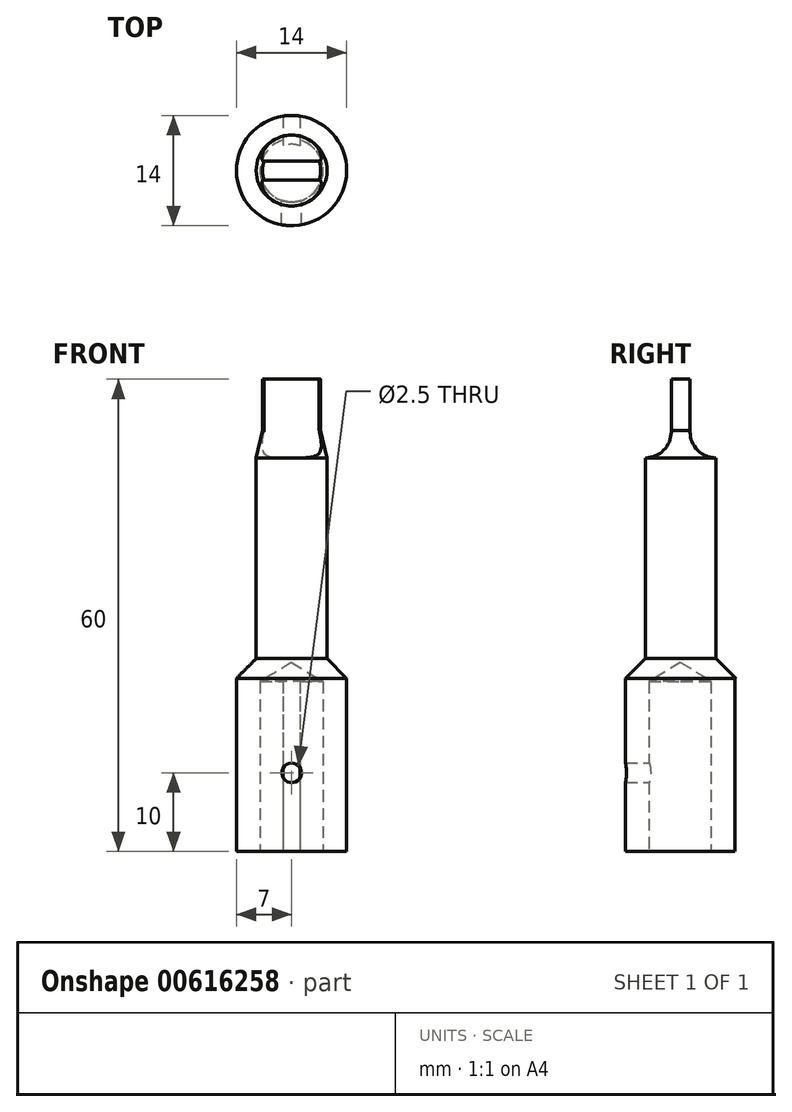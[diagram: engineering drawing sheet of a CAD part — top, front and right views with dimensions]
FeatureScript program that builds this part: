
annotation { "Feature Type Name" : "Feature", "Feature Type Description" : "" }
export const myFeature = defineFeature(function(context is Context, id is Id, definition is map)
    precondition{}
    {
        {
            var Q0;
            Q0=qCreatedBy(makeId("Front.planeOp"),FACE);
            var sketch = newSketch(context, id + "F0", { "sketchPlane" : qUnion([Q0])});
            skLineSegment(sketch, "E0", {"start": v(0, 0) * mm, "end": v(0, 60) * mm});
            skLineSegment(sketch, "E1", {"start": v(0, 60) * mm, "end": v(3.7, 60) * mm});
            skLineSegment(sketch, "E2", {"start": v(3.7, 60) * mm, "end": v(3.7, 53.5) * mm});
            skLineSegment(sketch, "E3", {"start": v(4.5, 50) * mm, "end": v(4.5, 24.5) * mm});
            skLineSegment(sketch, "E4", {"start": v(7, 22) * mm, "end": v(7, 0) * mm});
            skLineSegment(sketch, "E5", {"start": v(7, 0) * mm, "end": v(0, 0) * mm});
            skLineSegment(sketch, "E6", {"start": v(4.5, 50) * mm, "end": v(3.7, 53.5) * mm});
            skLineSegment(sketch, "E7", {"start": v(0, 0) * mm, "end": v(0, 83.24) * mm, "construction": true});
            skLineSegment(sketch, "E8", {"start": v(7, 22) * mm, "end": v(4.5, 24.5) * mm});
            skSolve(sketch);
        }
        {
            var Q0;
            Q0=makeQuery(id+"F0.imprint","IMPRINT",FACE,{"disambiguationData":[TD([[makeQuery(id+"F0.imprint","IMPRINT",EDGE,{"derivedFrom":sQuery(id+"F0.wireOp",EDGE,"E0")}),-1.0]])]});
            var Q1;
            Q1=sQuery(id+"F0.wireOp",EDGE,"E7");
            revolve(context, id + "F1", {"entities" : qUnion([Q0]), "axis" : qUnion([Q1]), "revolveType" : RevolveType.FULL});
        }
        {
            var Q0;
            Q0=makeQuery(id+"F1.opRevolve","SWEPT_FACE",FACE,{"disambiguationData":[OSD([sQuery(id+"F0.wireOp",EDGE,"E5")])]});
            var sketch = newSketch(context, id + "F2", { "sketchPlane" : qUnion([Q0])});
            skPoint(sketch, "E9", {"position": v(0, 0) * mm});
            skSolve(sketch);
        }
        {
            var Q0;
            Q0=sQuery(id+"F2.wireOp",VERTEX,"E9");
            var Q1;
            Q1=makeQuery(id+"F1.opRevolve","SWEPT_BODY",BODY,{"disambiguationData":[OSD([sQuery(id+"F0.wireOp",EDGE,"E0"),sQuery(id+"F0.wireOp",EDGE,"E1"),sQuery(id+"F0.wireOp",EDGE,"E2"),sQuery(id+"F0.wireOp",EDGE,"E3"),sQuery(id+"F0.wireOp",EDGE,"E4"),sQuery(id+"F0.wireOp",EDGE,"E5"),sQuery(id+"F0.wireOp",EDGE,"E6"),sQuery(id+"F0.wireOp",EDGE,"a6a139c0-5f27-4006-9743-78f47c573285.filletArc")])]});
            hole(context, id + "F3", {"style" : HoleStyle.SIMPLE, "endStyle" : HoleEndStyle.BLIND, "standardTappedOrClearance" : lookupTablePath({ "standard" : "ISO", "size" : "8", "type" : "Drilled" }), "standardBlindInLast" : lookupTablePath({ "standard" : "ISO", "size" : "8", "type" : "Drilled" }), "holeDiameter" : 8 * mm, "majorDiameter" : 5 * mm, "holeDepth" : 21.6 * mm, "isTappedThrough" : true, "tappedDepth" : 18.6 * mm, "tapClearance" : 3, "startFromSketch" : true, "locations" : qUnion([Q0]), "scope" : qUnion([Q1])});
        }
        {
            var Q0;
            Q0=qCreatedBy(makeId("Front.planeOp"),FACE);
            var sketch = newSketch(context, id + "F4", { "sketchPlane" : qUnion([Q0])});
            skLineSegment(sketch, "E10.bottom", {"start": v(1.1, 0) * mm, "end": v(-1.1, 0) * mm});
            skLineSegment(sketch, "E10.top", {"start": v(1.1, 22) * mm, "end": v(-1.1, 22) * mm});
            skLineSegment(sketch, "E10.left", {"start": v(1.1, 0) * mm, "end": v(1.1, 22) * mm});
            skLineSegment(sketch, "E10.right", {"start": v(-1.1, 0) * mm, "end": v(-1.1, 22) * mm});
            skPoint(sketch, "E11", {"position": v(0, 0) * mm});
            skSolve(sketch);
        }
        {
            var Q0;
            Q0 = qSketchRegion(id + "F4", true);
            extrude(context, id + "F5", {"entities" : qUnion([Q0]), "operationType" : NewBodyOperationType.REMOVE, "endBound" : BoundingType.THROUGH_ALL, "oppositeDirection" : true, "depth" : 25 * mm, "offsetDistance" : 25 * mm});
        }
        {
            var Q0;
            Q0=qCreatedBy(makeId("Front.planeOp"),FACE);
            var sketch = newSketch(context, id + "F6", { "sketchPlane" : qUnion([Q0])});
            skPoint(sketch, "E12", {"position": v(0, 10) * mm});
            skSolve(sketch);
        }
        {
            var Q0;
            Q0=sQuery(id+"F6.wireOp",VERTEX,"E12");
            var Q1;
            Q1=makeQuery(id+"F1.opRevolve","SWEPT_BODY",BODY,{"disambiguationData":[OSD([sQuery(id+"F0.wireOp",EDGE,"E0"),sQuery(id+"F0.wireOp",EDGE,"E1"),sQuery(id+"F0.wireOp",EDGE,"E2"),sQuery(id+"F0.wireOp",EDGE,"E3"),sQuery(id+"F0.wireOp",EDGE,"E4"),sQuery(id+"F0.wireOp",EDGE,"E5"),sQuery(id+"F0.wireOp",EDGE,"E6"),sQuery(id+"F0.wireOp",EDGE,"E8")])]});
            hole(context, id + "F7", {"style" : HoleStyle.SIMPLE, "endStyle" : HoleEndStyle.THROUGH, "oppositeDirection" : true, "holeDiameter" : 2.5 * mm, "majorDiameter" : 5 * mm, "isTappedThrough" : true, "tappedDepth" : 18.6 * mm, "tapClearance" : 3, "startFromSketch" : true, "locations" : qUnion([Q0]), "scope" : qUnion([Q1])});
        }
        {
            var Q0;
            Q0=qCreatedBy(makeId("Right.planeOp"),FACE);
            var sketch = newSketch(context, id + "F8", { "sketchPlane" : qUnion([Q0])});
            skLineSegment(sketch, "E13", {"start": v(0, 60.47) * mm, "end": v(0, 49.01) * mm, "construction": true});
            skLineSegment(sketch, "E14", {"start": v(1.2, 60) * mm, "end": v(1.2, 53.3) * mm});
            skLineSegment(sketch, "E15", {"start": v(4.5, 50) * mm, "end": v(6.91, 50) * mm});
            skLineSegment(sketch, "E16", {"start": v(6.91, 50) * mm, "end": v(6.91, 60) * mm});
            skLineSegment(sketch, "E17", {"start": v(6.91, 60) * mm, "end": v(1.2, 60) * mm});
            skPoint(sketch, "E18.visualSharp", {"position": v(1.2, 50) * mm});
            skArc(sketch, "E18.filletArc", {"start": v(1.2, 53.3) * mm, "mid": v(2.17, 50.97) * mm, "end": v(4.5, 50) * mm});
            skPoint(sketch, "E19.MirrorP", {"position": v(-1.2, 50) * mm});
            skLineSegment(sketch, "E20.MirrorCS", {"start": v(-1.2, 60) * mm, "end": v(-1.2, 53.3) * mm});
            skLineSegment(sketch, "E21.MirrorCS", {"start": v(-4.5, 50) * mm, "end": v(-6.91, 50) * mm});
            skLineSegment(sketch, "E22.MirrorCS", {"start": v(-6.91, 60) * mm, "end": v(-1.2, 60) * mm});
            skLineSegment(sketch, "E23.MirrorCS", {"start": v(-6.91, 50) * mm, "end": v(-6.91, 60) * mm});
            skArc(sketch, "E24.MirrorCS", {"start": v(-1.2, 53.3) * mm, "mid": v(-2.17, 50.97) * mm, "end": v(-4.5, 50) * mm});
            skSolve(sketch);
        }
        {
            var Q0;
            Q0=makeQuery(id+"F8.imprint","IMPRINT",FACE,{"disambiguationData":[TD([[makeQuery(id+"F8.imprint","IMPRINT",EDGE,{"derivedFrom":sQuery(id+"F8.wireOp",EDGE,"E20.MirrorCS")}),-1.0]])]});
            var Q1;
            Q1=makeQuery(id+"F8.imprint","IMPRINT",FACE,{"disambiguationData":[TD([[makeQuery(id+"F8.imprint","IMPRINT",EDGE,{"derivedFrom":sQuery(id+"F8.wireOp",EDGE,"E14")}),1.0]])]});
            extrude(context, id + "F9", {"entities" : qUnion([Q0, Q1]), "operationType" : NewBodyOperationType.REMOVE, "endBound" : BoundingType.SYMMETRIC, "oppositeDirection" : true, "depth" : 25 * mm, "offsetDistance" : 25 * mm});
        }
    });
